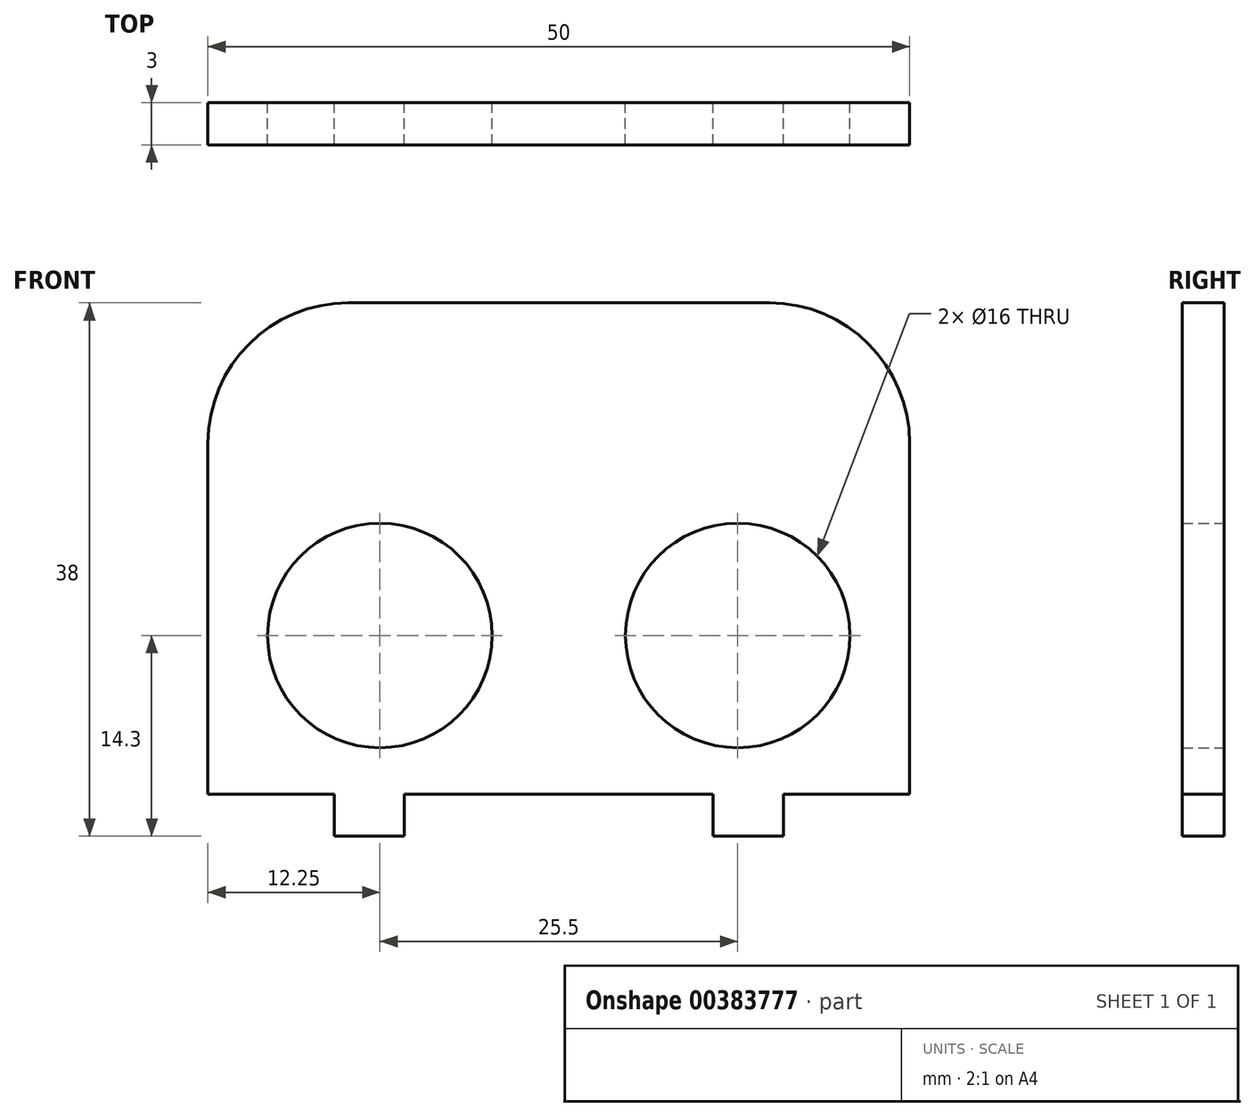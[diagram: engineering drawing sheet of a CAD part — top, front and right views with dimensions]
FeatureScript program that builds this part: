
annotation { "Feature Type Name" : "Feature", "Feature Type Description" : "" }
export const myFeature = defineFeature(function(context is Context, id is Id, definition is map)
    precondition{}
    {
        {
            var Q0;
            Q0=qCreatedBy(makeId("Front.planeOp"),FACE);
            var sketch = newSketch(context, id + "F0", { "sketchPlane" : qUnion([Q0])});
            skLineSegment(sketch, "E0.bottom", {"start": v(-15, 17.5) * mm, "end": v(15, 17.5) * mm});
            skLineSegment(sketch, "E0.top", {"start": v(-25, -17.5) * mm, "end": v(25, -17.5) * mm});
            skLineSegment(sketch, "E0.left", {"start": v(-25, 17.5) * mm, "end": v(-25, -17.5) * mm});
            skLineSegment(sketch, "E0.right", {"start": v(25, 7.5) * mm, "end": v(25, -17.5) * mm});
            skPoint(sketch, "E0.middle", {"position": v(0, 0) * mm});
            skLineSegment(sketch, "E1", {"start": v(-25, -17.5) * mm, "end": v(-25, 7.5) * mm, "construction": true});
            skLineSegment(sketch, "E2", {"start": v(0, -17.5) * mm, "end": v(0, 5) * mm, "construction": true});
            skLineSegment(sketch, "E3", {"start": v(0, 5) * mm, "end": v(-25, 5) * mm, "construction": true});
            skLineSegment(sketch, "E4", {"start": v(0, 5) * mm, "end": v(25, 5) * mm, "construction": true});
            skCircle(sketch, "E5", {"center": v(-12.75, -6.2) * mm, "radius": 8 * mm});
            skLineSegment(sketch, "E6", {"start": v(-12.75, -6.2) * mm, "end": v(-12.75, 5) * mm, "construction": true});
            skLineSegment(sketch, "E7.bottom", {"start": v(-11, -20.5) * mm, "end": v(-16, -20.5) * mm});
            skLineSegment(sketch, "E7.top", {"start": v(-11, -17.5) * mm, "end": v(-16, -17.5) * mm});
            skLineSegment(sketch, "E7.left", {"start": v(-11, -20.5) * mm, "end": v(-11, -17.5) * mm});
            skLineSegment(sketch, "E7.right", {"start": v(-16, -20.5) * mm, "end": v(-16, -17.5) * mm});
            skPoint(sketch, "E7.middle", {"position": v(-13.5, -19) * mm});
            skLineSegment(sketch, "E8.MirrorCS", {"start": v(16, -20.5) * mm, "end": v(16, -17.5) * mm});
            skLineSegment(sketch, "E9.MirrorCS", {"start": v(11, -20.5) * mm, "end": v(16, -20.5) * mm});
            skLineSegment(sketch, "E10.MirrorCS", {"start": v(11, -20.5) * mm, "end": v(11, -17.5) * mm});
            skLineSegment(sketch, "E11.MirrorCS", {"start": v(11, -17.5) * mm, "end": v(16, -17.5) * mm});
            skCircle(sketch, "E12.MirrorC", {"center": v(12.75, -6.2) * mm, "radius": 8 * mm});
            skLineSegment(sketch, "E13", {"start": v(12.75, -6.2) * mm, "end": v(0, -6.2) * mm, "construction": true});
            skLineSegment(sketch, "E14", {"start": v(0, -6.2) * mm, "end": v(0, -15.47) * mm, "construction": true});
            skLineSegment(sketch, "E15", {"start": v(4.75, -6.2) * mm, "end": v(-4.75, -6.2) * mm, "construction": true});
            skPoint(sketch, "E16.visualSharp", {"position": v(-25, 17.5) * mm});
            skArc(sketch, "E16.filletArc", {"start": v(-15, 17.5) * mm, "mid": v(-22.07, 14.57) * mm, "end": v(-25, 7.5) * mm});
            skPoint(sketch, "E17.visualSharp", {"position": v(25, 17.5) * mm});
            skArc(sketch, "E17.filletArc", {"start": v(25, 7.5) * mm, "mid": v(22.07, 14.57) * mm, "end": v(15, 17.5) * mm});
            skSolve(sketch);
        }
        {
            var Q0;
            Q0=makeQuery(id+"F0.imprint","IMPRINT",FACE,{"disambiguationData":[TD([[makeQuery(id+"F0.imprint","IMPRINT",EDGE,{"derivedFrom":sQuery(id+"F0.wireOp",EDGE,"E0.bottom")}),-1.0]])]});
            var Q1;
            Q1=makeQuery(id+"F0.imprint","IMPRINT",FACE,{"disambiguationData":[TD([[makeQuery(id+"F0.imprint","IMPRINT",EDGE,{"derivedFrom":sQuery(id+"F0.wireOp",EDGE,"E7.bottom")}),-1.0]])]});
            var Q2;
            Q2=makeQuery(id+"F0.imprint","IMPRINT",FACE,{"disambiguationData":[TD([[makeQuery(id+"F0.imprint","IMPRINT",EDGE,{"derivedFrom":sQuery(id+"F0.wireOp",EDGE,"E8.MirrorCS")}),1.0]])]});
            extrude(context, id + "F1", {"entities" : qUnion([Q0, Q1, Q2]), "depth" : 3 * mm});
        }
    });
